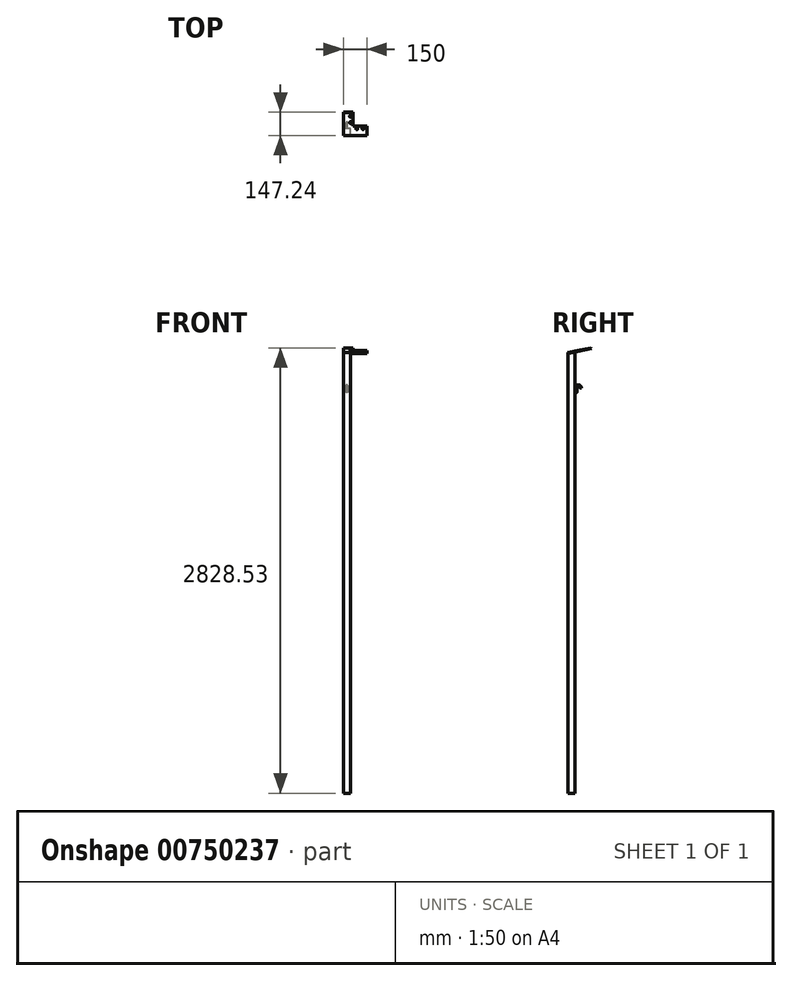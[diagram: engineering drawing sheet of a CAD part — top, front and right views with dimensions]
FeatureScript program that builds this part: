
annotation { "Feature Type Name" : "Feature", "Feature Type Description" : "" }
export const myFeature = defineFeature(function(context is Context, id is Id, definition is map)
    precondition{}
    {
        {
            var Q0;
            Q0=qCreatedBy(makeId("Top.planeOp"),FACE);
            var sketch = newSketch(context, id + "F0", { "sketchPlane" : qUnion([Q0])});
            skLineSegment(sketch, "E0.bottom", {"start": v(22.5, -22.5) * mm, "end": v(-22.5, -22.5) * mm});
            skLineSegment(sketch, "E0.top", {"start": v(22.5, 22.5) * mm, "end": v(-22.5, 22.5) * mm});
            skLineSegment(sketch, "E0.left", {"start": v(22.5, -22.5) * mm, "end": v(22.5, 22.5) * mm});
            skLineSegment(sketch, "E0.right", {"start": v(-22.5, -22.5) * mm, "end": v(-22.5, 22.5) * mm});
            skPoint(sketch, "E0.middle", {"position": v(0, 0) * mm});
            skSolve(sketch);
        }
        {
            var Q0;
            Q0 = qSketchRegion(id + "F0", true);
            extrude(context, id + "F1", {"entities" : qUnion([Q0]), "depth" : 2795 * mm, "offsetDistance" : 25 * mm});
        }
        {
            var Q0;
            Q0=makeQuery(id+"F1.opExtrude","CAP_EDGE",EDGE,{"disambiguationData":[OSD([sQuery(id+"F0.wireOp",EDGE,"E0.bottom")])],"isStart":false});
            cPlane(context, id + "F2", {"entities" : qUnion([Q0]), "cplaneType" : CPlaneType.LINE_ANGLE, "offset" : 25 * mm, "angle" : 79 * degree, "width" : 150 * mm, "height" : 150 * mm});
        }
        {
            var Q0;
            Q0=qCreatedBy(id+"F2.planeOp",FACE);
            var sketch = newSketch(context, id + "F3", { "sketchPlane" : qUnion([Q0])});
            skLineSegment(sketch, "E1.bottom", {"start": v(-22.5, 511.22) * mm, "end": v(37.5, 511.22) * mm});
            skLineSegment(sketch, "E1.top", {"start": v(-22.5, 661.22) * mm, "end": v(37.5, 661.22) * mm});
            skLineSegment(sketch, "E1.left", {"start": v(-22.5, 511.22) * mm, "end": v(-22.5, 661.22) * mm});
            skLineSegment(sketch, "E1.right", {"start": v(37.5, 511.22) * mm, "end": v(37.5, 661.22) * mm});
            skLineSegment(sketch, "E2.bottom", {"start": v(37.5, 511.22) * mm, "end": v(127.5, 511.22) * mm});
            skLineSegment(sketch, "E2.top", {"start": v(37.5, 571.22) * mm, "end": v(127.5, 571.22) * mm});
            skLineSegment(sketch, "E2.left", {"start": v(37.5, 511.22) * mm, "end": v(37.5, 571.22) * mm});
            skLineSegment(sketch, "E2.right", {"start": v(127.5, 511.22) * mm, "end": v(127.5, 571.22) * mm});
            skSolve(sketch);
        }
        {
            var Q0;
            Q0 = qSketchRegion(id + "F3", true);
            extrude(context, id + "F4", {"entities" : qUnion([Q0]), "depth" : 5 * mm, "offsetDistance" : 25 * mm});
        }
        {
            var Q0;
            Q0=makeQuery(id+"F1.opExtrude","SWEPT_FACE",FACE,{"disambiguationData":[OSD([sQuery(id+"F0.wireOp",EDGE,"E0.left")])]});
            var sketch = newSketch(context, id + "F5", { "sketchPlane" : qUnion([Q0])});
            skLineSegment(sketch, "E3", {"start": v(22.5, 2795) * mm, "end": v(22.5, 2803.75) * mm});
            skLineSegment(sketch, "E4", {"start": v(22.5, 2803.75) * mm, "end": v(-22.5, 2795) * mm});
            skLineSegment(sketch, "E5", {"start": v(-22.5, 2795) * mm, "end": v(22.5, 2795) * mm});
            skSolve(sketch);
        }
        {
            var Q0;
            Q0 = qSketchRegion(id + "F5", true);
            extrude(context, id + "F6", {"entities" : qUnion([Q0]), "oppositeDirection" : true, "depth" : 45 * mm, "offsetDistance" : 25 * mm});
        }
        {
            var Q0;
            Q0=makeQuery(id+"F1.opExtrude","SWEPT_BODY",BODY,{"disambiguationData":[OSD([sQuery(id+"F0.wireOp",EDGE,"E0.bottom"),sQuery(id+"F0.wireOp",EDGE,"E0.top"),sQuery(id+"F0.wireOp",EDGE,"E0.left"),sQuery(id+"F0.wireOp",EDGE,"E0.right")])]});
            var Q1;
            Q1=makeQuery(id+"F6.opExtrude","SWEPT_BODY",BODY,{"disambiguationData":[OSD([sQuery(id+"F5.wireOp",EDGE,"E3"),sQuery(id+"F5.wireOp",EDGE,"E4"),sQuery(id+"F5.wireOp",EDGE,"E5")])]});
            var Q2;
            Q2=makeQuery(id+"F4.opExtrude","SWEPT_BODY",BODY,{"disambiguationData":[OSD([sQuery(id+"F3.wireOp",EDGE,"E1.bottom"),sQuery(id+"F3.wireOp",EDGE,"E1.top"),sQuery(id+"F3.wireOp",EDGE,"E1.left"),sQuery(id+"F3.wireOp",EDGE,"E1.right"),sQuery(id+"F3.wireOp",EDGE,"E2.bottom"),sQuery(id+"F3.wireOp",EDGE,"E2.top"),sQuery(id+"F3.wireOp",EDGE,"E2.right")])]});
            booleanBodies(context, id + "F7", {"operationType" : BooleanOperationType.UNION, "tools" : qUnion([Q0, Q1, Q2])});
        }
        {
            var Q0;
            Q0=makeQuery(id+"F7.opBoolean","MERGE",FACE,{"derivedFrom":[makeQuery(id+"F1.opExtrude","SWEPT_FACE",FACE,{"disambiguationData":[OSD([sQuery(id+"F0.wireOp",EDGE,"E0.right")])]}),makeQuery(id+"F4.opExtrude","SWEPT_FACE",FACE,{"disambiguationData":[OSD([sQuery(id+"F3.wireOp",EDGE,"E1.left")])]}),makeQuery(id+"F6.opExtrude","CAP_FACE",FACE,{"disambiguationData":[OSD([sQuery(id+"F5.wireOp",EDGE,"E3"),sQuery(id+"F5.wireOp",EDGE,"E4"),sQuery(id+"F5.wireOp",EDGE,"E5")])],"isStart":false})]});
            var sketch = newSketch(context, id + "F8", { "sketchPlane" : qUnion([Q0])});
            skLineSegment(sketch, "E6", {"start": v(9.37, 2795) * mm, "end": v(22.5, 2795) * mm});
            skLineSegment(sketch, "E7.bottom", {"start": v(22.5, 2795) * mm, "end": v(25.28, 2795) * mm});
            skLineSegment(sketch, "E7.top", {"start": v(22.5, 2800.7) * mm, "end": v(25.28, 2800.7) * mm});
            skLineSegment(sketch, "E7.left", {"start": v(22.5, 2795) * mm, "end": v(22.5, 2800.7) * mm});
            skLineSegment(sketch, "E7.right", {"start": v(25.28, 2795) * mm, "end": v(25.28, 2800.7) * mm});
            skSolve(sketch);
        }
        {
            var Q0;
            Q0 = qSketchRegion(id + "F8", true);
            var Q1;
            Q1=makeQuery(id+"F4.opExtrude","SWEPT_FACE",FACE,{"disambiguationData":[OSD([sQuery(id+"F3.wireOp",EDGE,"E2.right")])]});
            extrude(context, id + "F9", {"entities" : qUnion([Q0]), "operationType" : NewBodyOperationType.REMOVE, "endBound" : BoundingType.UP_TO_SURFACE, "oppositeDirection" : true, "depth" : 156.8 * mm, "endBoundEntityFace" : qUnion([Q1]), "offsetDistance" : 25 * mm});
        }
        {
            var Q0;
            Q0=makeQuery(id+"F4.opExtrude","CAP_FACE",FACE,{"disambiguationData":[OSD([sQuery(id+"F3.wireOp",EDGE,"E1.bottom"),sQuery(id+"F3.wireOp",EDGE,"E1.top"),sQuery(id+"F3.wireOp",EDGE,"E1.left"),sQuery(id+"F3.wireOp",EDGE,"E1.right"),sQuery(id+"F3.wireOp",EDGE,"E2.bottom"),sQuery(id+"F3.wireOp",EDGE,"E2.top"),sQuery(id+"F3.wireOp",EDGE,"E2.right")])],"isStart":false});
            var sketch = newSketch(context, id + "F10", { "sketchPlane" : qUnion([Q0])});
            skLineSegment(sketch, "E8", {"start": v(127.5, 571.22) * mm, "end": v(102.5, 571.22) * mm});
            skLineSegment(sketch, "E9", {"start": v(102.5, 571.22) * mm, "end": v(102.5, 556.22) * mm});
            skLineSegment(sketch, "E10", {"start": v(102.5, 556.22) * mm, "end": v(62.5, 556.22) * mm});
            skCircle(sketch, "E11", {"center": v(102.5, 556.22) * mm, "radius": 6 * mm});
            skCircle(sketch, "E12", {"center": v(62.5, 556.22) * mm, "radius": 6 * mm});
            skLineSegment(sketch, "E13", {"start": v(37.5, 661.22) * mm, "end": v(37.5, 636.22) * mm});
            skLineSegment(sketch, "E14", {"start": v(37.5, 636.22) * mm, "end": v(22.5, 636.22) * mm});
            skLineSegment(sketch, "E15", {"start": v(22.5, 636.22) * mm, "end": v(22.5, 596.22) * mm});
            skCircle(sketch, "E16", {"center": v(22.5, 636.22) * mm, "radius": 6 * mm});
            skCircle(sketch, "E17", {"center": v(22.5, 596.22) * mm, "radius": 6 * mm});
            skLineSegment(sketch, "E18", {"start": v(-22.5, 661.22) * mm, "end": v(-22.5, 512.2) * mm});
            skSolve(sketch);
        }
        {
            var Q0;
            Q0 = qSketchRegion(id + "F10", true);
            var Q1;
            Q1=makeQuery(id+"F4.opExtrude","CAP_FACE",FACE,{"disambiguationData":[OSD([sQuery(id+"F3.wireOp",EDGE,"E1.bottom"),sQuery(id+"F3.wireOp",EDGE,"E1.top"),sQuery(id+"F3.wireOp",EDGE,"E1.left"),sQuery(id+"F3.wireOp",EDGE,"E1.right"),sQuery(id+"F3.wireOp",EDGE,"E2.bottom"),sQuery(id+"F3.wireOp",EDGE,"E2.top"),sQuery(id+"F3.wireOp",EDGE,"E2.right")])],"isStart":true});
            extrude(context, id + "F11", {"entities" : qUnion([Q0]), "operationType" : NewBodyOperationType.REMOVE, "endBound" : BoundingType.UP_TO_SURFACE, "oppositeDirection" : true, "depth" : 25 * mm, "endBoundEntityFace" : qUnion([Q1]), "offsetDistance" : 25 * mm});
        }
        {
            var Q0;
            Q0=qCreatedBy(makeId("Top.planeOp"),FACE);
            cPlane(context, id + "F12", {"entities" : qUnion([Q0]), "cplaneType" : CPlaneType.OFFSET, "offset" : 2545 * mm, "width" : 150 * mm, "height" : 150 * mm});
        }
        {
            var Q0;
            Q0=qCreatedBy(id+"F12.planeOp",FACE);
            var sketch = newSketch(context, id + "F13", { "sketchPlane" : qUnion([Q0])});
            skLineSegment(sketch, "E19", {"start": v(0, 22.5) * mm, "end": v(0, 27.5) * mm});
            skCircle(sketch, "E20", {"center": v(0, 27.5) * mm, "radius": 5 * mm});
            skLineSegment(sketch, "E21", {"start": v(0, 27.5) * mm, "end": v(5, 27.5) * mm});
            skLineSegment(sketch, "E22", {"start": v(5, 27.5) * mm, "end": v(5, 22.5) * mm});
            skLineSegment(sketch, "E23", {"start": v(0, 27.5) * mm, "end": v(-5, 27.5) * mm});
            skLineSegment(sketch, "E24", {"start": v(-5, 27.5) * mm, "end": v(-5, 22.5) * mm});
            skLineSegment(sketch, "E25", {"start": v(5, 22.5) * mm, "end": v(-5, 22.5) * mm});
            skSolve(sketch);
        }
        {
            var Q0;
            Q0=qCreatedBy(makeId("Right.planeOp"),FACE);
            var sketch = newSketch(context, id + "F14", { "sketchPlane" : qUnion([Q0])});
            skLineSegment(sketch, "E26", {"start": v(27.5, 2545) * mm, "end": v(27.5, 2575) * mm});
            skLineSegment(sketch, "E27", {"start": v(27.5, 2575) * mm, "end": v(57.5, 2575) * mm});
            skArc(sketch, "E28", {"start": v(57.5, 2575) * mm, "mid": v(42.5, 2590) * mm, "end": v(27.5, 2575) * mm});
            skSolve(sketch);
        }
        {
            var Q0;
            Q0 = qSketchRegion(id + "F13", true);
            extrude(context, id + "F15", {"entities" : qUnion([Q0]), "operationType" : NewBodyOperationType.ADD, "depth" : 30 * mm, "offsetDistance" : 25 * mm});
        }
        {
            var Q0;
            Q0=makeQuery(id+"F15.opExtrude","CAP_FACE",FACE,{"disambiguationData":[OSD([sQuery(id+"F13.wireOp",EDGE,"E20"),sQuery(id+"F13.wireOp",EDGE,"E22"),sQuery(id+"F13.wireOp",EDGE,"E24"),sQuery(id+"F13.wireOp",EDGE,"E25")])],"isStart":false});
            var sketch = newSketch(context, id + "F16", { "sketchPlane" : qUnion([Q0])});
            skArc(sketch, "E29.0", {"start": v(5, 27.5) * mm, "mid": v(0, 32.5) * mm, "end": v(-5, 27.5) * mm});
            skLineSegment(sketch, "E30", {"start": v(0, 27.5) * mm, "end": v(-5, 27.5) * mm, "construction": true});
            skArc(sketch, "E31.MirrorCS", {"start": v(5, 27.5) * mm, "mid": v(0, 22.5) * mm, "end": v(-5, 27.5) * mm});
            skSolve(sketch);
        }
        {
            var Q0;
            {var subQ0=sQuery(id+"F16.wireOp",EDGE,"E29.0");Q0=makeQuery(id+"F16.imprint","IMPRINT",FACE,{"disambiguationData":[TD([[makeQuery(id+"F16.imprint","IMPRINT",EDGE,{"derivedFrom":subQ0}),1.0]])]});}
            var Q1;
            Q1=sQuery(id+"F14.wireOp",EDGE,"E28");
            sweep(context, id + "F17", {"operationType" : NewBodyOperationType.ADD, "profiles" : qUnion([Q0]), "path" : qUnion([Q1])});
        }
    });
